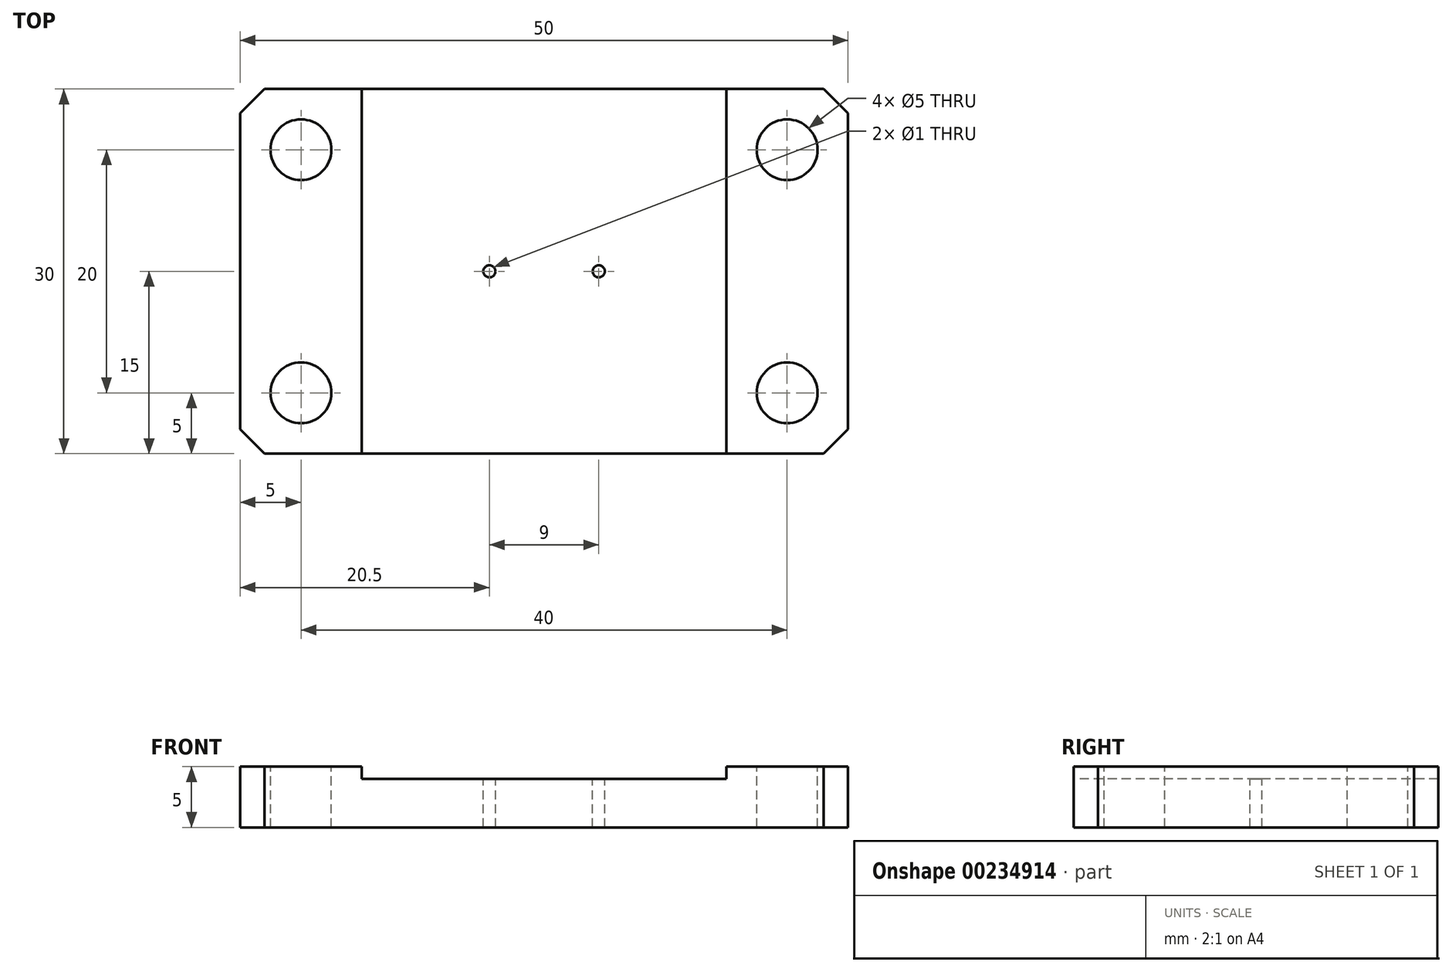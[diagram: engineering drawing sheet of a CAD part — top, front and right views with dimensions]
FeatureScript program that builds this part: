
annotation { "Feature Type Name" : "Feature", "Feature Type Description" : "" }
export const myFeature = defineFeature(function(context is Context, id is Id, definition is map)
    precondition{}
    {
        {
            var Q0;
            Q0=qCreatedBy(makeId("Top.planeOp"),FACE);
            var sketch = newSketch(context, id + "F0", { "sketchPlane" : qUnion([Q0])});
            skLineSegment(sketch, "E0.bottom", {"start": v(25, 15) * mm, "end": v(-25, 15) * mm});
            skLineSegment(sketch, "E0.top", {"start": v(25, -15) * mm, "end": v(-25, -15) * mm});
            skLineSegment(sketch, "E0.left", {"start": v(25, 15) * mm, "end": v(25, -15) * mm});
            skLineSegment(sketch, "E0.right", {"start": v(-25, 15) * mm, "end": v(-25, -15) * mm});
            skPoint(sketch, "E0.middle", {"position": v(0, 0) * mm});
            skSolve(sketch);
        }
        {
            var Q0;
            Q0 = qSketchRegion(id + "F0", true);
            extrude(context, id + "F1", {"entities" : qUnion([Q0]), "depth" : 5 * mm});
        }
        {
            var Q0;
            Q0=makeQuery(id+"F1.opExtrude","CAP_FACE",FACE,{"disambiguationData":[OSD([sQuery(id+"F0.wireOp",EDGE,"E0.bottom"),sQuery(id+"F0.wireOp",EDGE,"E0.top"),sQuery(id+"F0.wireOp",EDGE,"E0.left"),sQuery(id+"F0.wireOp",EDGE,"E0.right")])],"isStart":false});
            var sketch = newSketch(context, id + "F2", { "sketchPlane" : qUnion([Q0])});
            skLineSegment(sketch, "E1.bottom", {"start": v(15, 15) * mm, "end": v(-15, 15) * mm});
            skLineSegment(sketch, "E1.top", {"start": v(15, -15) * mm, "end": v(-15, -15) * mm});
            skLineSegment(sketch, "E1.left", {"start": v(15, 15) * mm, "end": v(15, -15) * mm});
            skLineSegment(sketch, "E1.right", {"start": v(-15, 15) * mm, "end": v(-15, -15) * mm});
            skPoint(sketch, "E1.middle", {"position": v(0, 0) * mm});
            skSolve(sketch);
        }
        {
            var Q0;
            Q0 = qSketchRegion(id + "F2", true);
            extrude(context, id + "F3", {"entities" : qUnion([Q0]), "operationType" : NewBodyOperationType.REMOVE, "oppositeDirection" : true, "depth" : 1 * mm});
        }
        {
            var Q0;
            Q0=makeQuery(id+"F1.opExtrude","SWEPT_EDGE",EDGE,{"disambiguationData":[OSD([sQuery(id+"F0.wireOp",EDGE,"E0.bottom"),sQuery(id+"F0.wireOp",EDGE,"E0.right")])]});
            var Q1;
            Q1=makeQuery(id+"F1.opExtrude","SWEPT_EDGE",EDGE,{"disambiguationData":[OSD([sQuery(id+"F0.wireOp",EDGE,"E0.top"),sQuery(id+"F0.wireOp",EDGE,"E0.right")])]});
            var Q2;
            Q2=makeQuery(id+"F1.opExtrude","SWEPT_EDGE",EDGE,{"disambiguationData":[OSD([sQuery(id+"F0.wireOp",EDGE,"E0.top"),sQuery(id+"F0.wireOp",EDGE,"E0.left")])]});
            var Q3;
            Q3=makeQuery(id+"F1.opExtrude","SWEPT_EDGE",EDGE,{"disambiguationData":[OSD([sQuery(id+"F0.wireOp",EDGE,"E0.bottom"),sQuery(id+"F0.wireOp",EDGE,"E0.left")])]});
            chamfer(context, id + "F4", {"entities" : qUnion([Q0, Q1, Q2, Q3]), "width" : 2 * mm, "tangentPropagation" : true});
        }
        {
            var Q0;
            {var subQ0=sQuery(id+"F0.wireOp",EDGE,"E0.bottom");var subQ1=sQuery(id+"F0.wireOp",EDGE,"E0.top");var subQ2=sQuery(id+"F0.wireOp",EDGE,"E0.right");Q0=makeQuery(id+"F3.boolean.opBoolean","SPLIT",FACE,{"disambiguationData":[TD([makeQuery(id+"F1.opExtrude","SWEPT_FACE",FACE,{"disambiguationData":[OSD([subQ2])]})])],"derivedFrom":makeQuery(id+"F1.opExtrude","CAP_FACE",FACE,{"disambiguationData":[OSD([subQ0,subQ1,sQuery(id+"F0.wireOp",EDGE,"E0.left"),subQ2])],"isStart":false})});}
            var sketch = newSketch(context, id + "F5", { "sketchPlane" : qUnion([Q0])});
            skLineSegment(sketch, "E2", {"start": v(-25, 0) * mm, "end": v(-15, 0) * mm, "construction": true});
            skLineSegment(sketch, "E3", {"start": v(-20, 0) * mm, "end": v(-20, 15) * mm, "construction": true});
            skLineSegment(sketch, "E4", {"start": v(-20, 0) * mm, "end": v(-20, -15) * mm, "construction": true});
            skPoint(sketch, "E4.endSnap0", {"position": v(-19, -15) * mm});
            skCircle(sketch, "E5", {"center": v(-20, 10) * mm, "radius": 2.5 * mm});
            skCircle(sketch, "E6", {"center": v(-20, -10) * mm, "radius": 2.5 * mm});
            skLineSegment(sketch, "E7", {"start": v(0, -1) * mm, "end": v(0, -21) * mm, "construction": true});
            skLineSegment(sketch, "E8", {"start": v(0, -1) * mm, "end": v(0, 19) * mm, "construction": true});
            skLineSegment(sketch, "E9.MirrorCS", {"start": v(20, 0) * mm, "end": v(20, 15) * mm, "construction": true});
            skLineSegment(sketch, "E10.MirrorCS", {"start": v(20, 0) * mm, "end": v(20, -15) * mm, "construction": true});
            skLineSegment(sketch, "E11.MirrorCS", {"start": v(25, 0) * mm, "end": v(15, 0) * mm, "construction": true});
            skPoint(sketch, "E12.MirrorP", {"position": v(19, -15) * mm});
            skCircle(sketch, "E13.MirrorC", {"center": v(20, -10) * mm, "radius": 2.5 * mm});
            skCircle(sketch, "E14.MirrorC", {"center": v(20, 10) * mm, "radius": 2.5 * mm});
            skSolve(sketch);
        }
        {
            var Q0;
            Q0 = qSketchRegion(id + "F5", true);
            extrude(context, id + "F6", {"entities" : qUnion([Q0]), "operationType" : NewBodyOperationType.REMOVE, "oppositeDirection" : true, "depth" : 25 * mm});
        }
        {
            var Q0;
            Q0=makeQuery(id+"F3.boolean.opBoolean","COPY",FACE,{"derivedFrom":makeQuery(id+"F3.opExtrude","CAP_FACE",FACE,{"disambiguationData":[OSD([sQuery(id+"F2.wireOp",EDGE,"E1.bottom"),sQuery(id+"F2.wireOp",EDGE,"E1.top"),sQuery(id+"F2.wireOp",EDGE,"E1.left"),sQuery(id+"F2.wireOp",EDGE,"E1.right")])],"isStart":false})});
            var sketch = newSketch(context, id + "F7", { "sketchPlane" : qUnion([Q0])});
            skCircle(sketch, "E15", {"center": v(0, 0) * mm, "radius": 5 * mm, "construction": true});
            skCircle(sketch, "E16", {"center": v(0, 0) * mm, "radius": 4.5 * mm, "construction": true});
            skCircle(sketch, "E17", {"center": v(-4.5, 0) * mm, "radius": 0.5 * mm});
            skCircle(sketch, "E18", {"center": v(4.5, 0) * mm, "radius": 0.5 * mm});
            skSolve(sketch);
        }
        {
            var Q0;
            Q0 = qSketchRegion(id + "F7", true);
            extrude(context, id + "F8", {"entities" : qUnion([Q0]), "operationType" : NewBodyOperationType.REMOVE, "oppositeDirection" : true, "depth" : 25 * mm});
        }
    });
